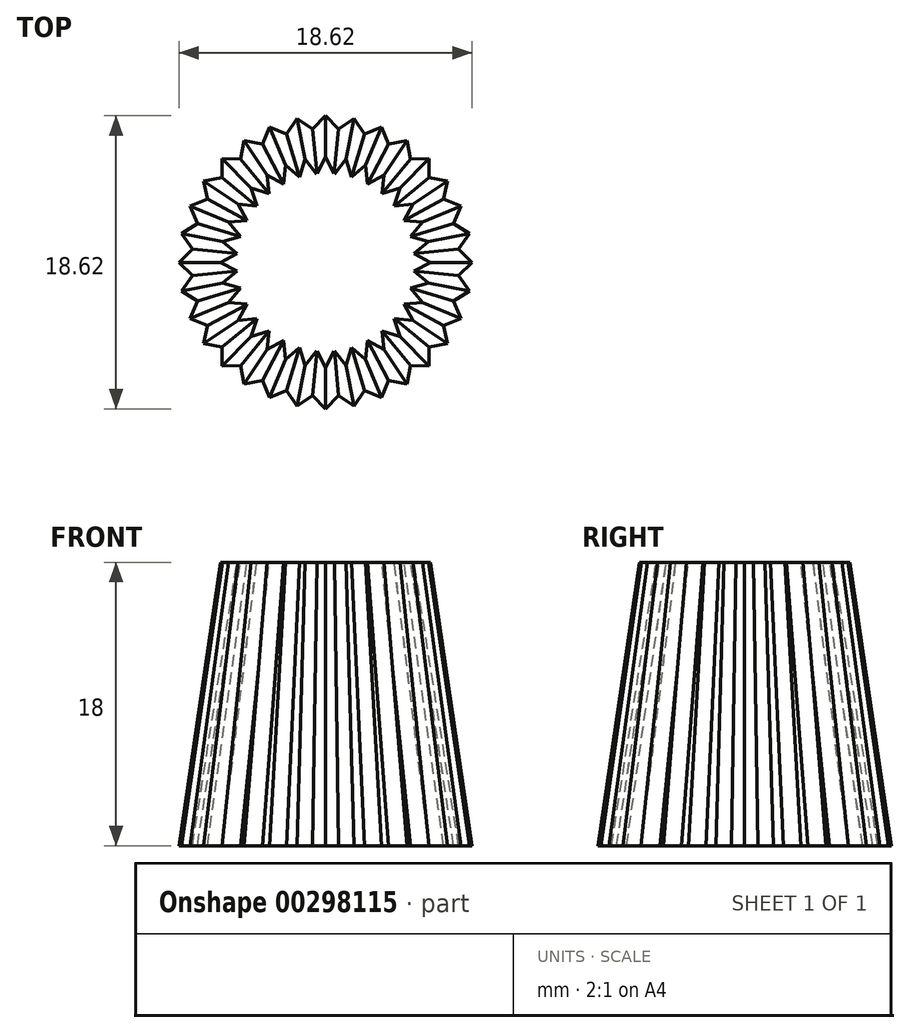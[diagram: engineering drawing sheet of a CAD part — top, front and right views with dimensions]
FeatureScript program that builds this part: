
annotation { "Feature Type Name" : "Feature", "Feature Type Description" : "" }
export const myFeature = defineFeature(function(context is Context, id is Id, definition is map)
    precondition{}
    {
        {
            var Q0;
            Q0=qCreatedBy(makeId("Top.planeOp"),FACE);
            var sketch = newSketch(context, id + "F0", { "sketchPlane" : qUnion([Q0])});
            skCircle(sketch, "E0", {"center": v(0, 0) * mm, "radius": 8.5 * mm});
            skSolve(sketch);
        }
        {
            var Q0;
            Q0=makeQuery(id+"F0.imprint","IMPRINT",FACE,{"disambiguationData":[TD([[makeQuery(id+"F0.imprint","IMPRINT",EDGE,{"derivedFrom":sQuery(id+"F0.wireOp",EDGE,"E0")}),1.0]])]});
            extrude(context, id + "F1", {"entities" : qUnion([Q0]), "depth" : 18 * mm, "hasDraft" : true, "draftAngle" : 9 * degree, "draftPullDirection" : true});
        }
        {
            var Q0;
            Q0=qCreatedBy(makeId("Top.planeOp"),FACE);
            var sketch = newSketch(context, id + "F2", { "sketchPlane" : qUnion([Q0])});
            skLineSegment(sketch, "E1", {"start": v(0, 9.31) * mm, "end": v(-0.83, 8.46) * mm});
            skLineSegment(sketch, "E2", {"start": v(-0.83, 8.46) * mm, "end": v(0.83, 8.46) * mm});
            skLineSegment(sketch, "E3", {"start": v(0.83, 8.46) * mm, "end": v(0, 9.31) * mm});
            skSolve(sketch);
        }
        {
            var Q0;
            Q0=makeQuery(id+"F1.opExtrude","CAP_FACE",FACE,{"disambiguationData":[OSD([sQuery(id+"F0.wireOp",EDGE,"E0")])],"isStart":false});
            var sketch = newSketch(context, id + "F3", { "sketchPlane" : qUnion([Q0])});
            skLineSegment(sketch, "E4", {"start": v(0, 6.68) * mm, "end": v(-0.55, 5.62) * mm});
            skLineSegment(sketch, "E5", {"start": v(-0.55, 5.62) * mm, "end": v(0.55, 5.62) * mm});
            skLineSegment(sketch, "E6", {"start": v(0.55, 5.62) * mm, "end": v(0, 6.68) * mm});
            skSolve(sketch);
        }
        {
            var Q1;
            Q1=makeQuery(id+"F2.imprint","IMPRINT",FACE,{"disambiguationData":[TD([[makeQuery(id+"F2.imprint","IMPRINT",EDGE,{"derivedFrom":sQuery(id+"F2.wireOp",EDGE,"E1")}),1.0]])]});
            var Q2;
            {var subQ0=sQuery(id+"F3.wireOp",EDGE,"E4");Q2=makeQuery(id+"F3.imprint","IMPRINT",FACE,{"disambiguationData":[TD([[makeQuery(id+"F3.imprint","IMPRINT",EDGE,{"derivedFrom":subQ0}),1.0]])]});}
            loft(context, id + "F4", {"sheetProfilesArray" : [{ "sheetProfileEntities" : qUnion([Q1]) }, { "sheetProfileEntities" : qUnion([Q2]) }]});
        }
        {
            var Q0;
            Q0=qCreatedBy(makeId("Front.planeOp"),FACE);
            var sketch = newSketch(context, id + "F5", { "sketchPlane" : qUnion([Q0])});
            skLineSegment(sketch, "E7", {"start": v(0, 24.88) * mm, "end": v(0, -4.9) * mm, "construction": true});
            skSolve(sketch);
        }
        {
            var Q0;
            {var subQ0=sQuery(id+"F3.wireOp",EDGE,"E4");Q0=makeQuery(id+"F4.opLoft","SWEPT_BODY",BODY,{"disambiguationData":[OSD([makeQuery(id+"F2.imprint","IMPRINT",FACE,{"disambiguationData":[TD([[makeQuery(id+"F2.imprint","IMPRINT",EDGE,{"derivedFrom":sQuery(id+"F2.wireOp",EDGE,"E1")}),1.0]])]}),makeQuery(id+"F3.imprint","IMPRINT",FACE,{"disambiguationData":[TD([[makeQuery(id+"F3.imprint","IMPRINT",EDGE,{"derivedFrom":subQ0}),1.0]])]})])]});}
            var Q1;
            Q1=sQuery(id+"F5.wireOp",EDGE,"E7");
            circularPattern(context, id + "F6", {"operationType" : NewBodyOperationType.ADD, "entities" : qUnion([Q0]), "axis" : qUnion([Q1]), "angle" : 360 * degree, "instanceCount" : 32, "equalSpace" : true});
        }
    });
